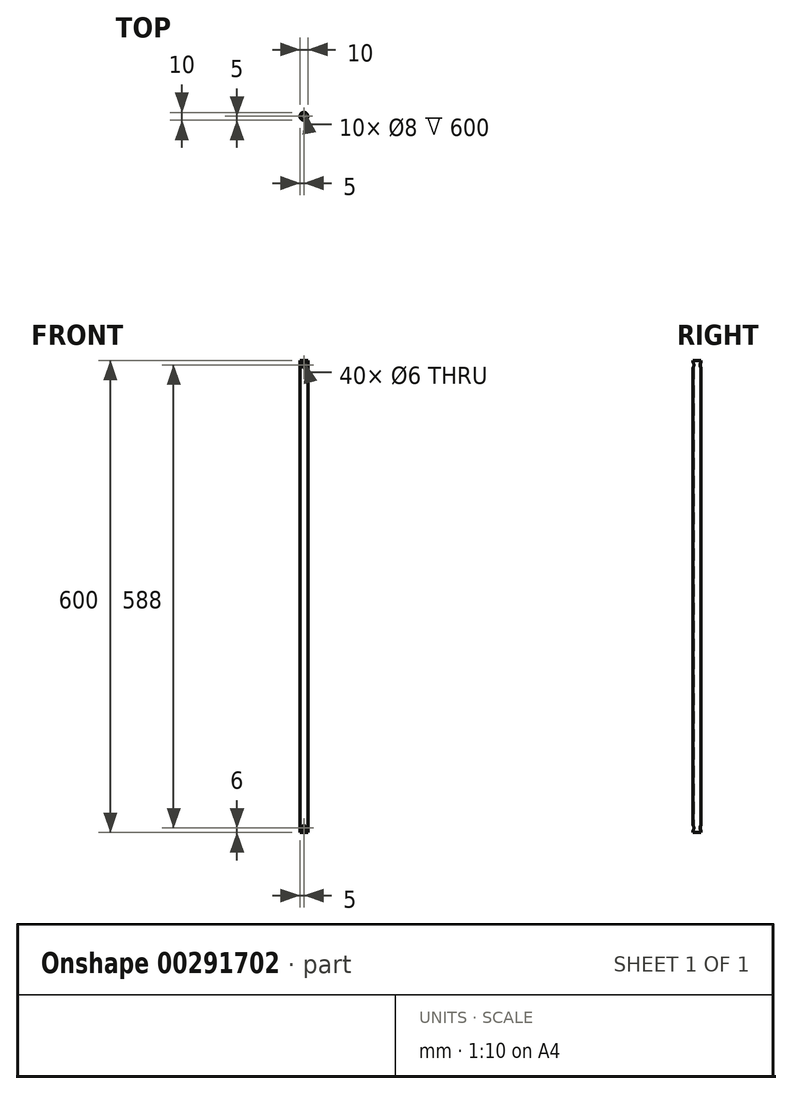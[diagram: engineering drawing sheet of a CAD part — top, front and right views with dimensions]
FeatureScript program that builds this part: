
annotation { "Feature Type Name" : "Feature", "Feature Type Description" : "" }
export const myFeature = defineFeature(function(context is Context, id is Id, definition is map)
    precondition{}
    {
        {
            var Q0;
            Q0=qCreatedBy(makeId("Top.planeOp"),FACE);
            var sketch = newSketch(context, id + "F0", { "sketchPlane" : qUnion([Q0])});
            skCircle(sketch, "E0", {"center": v(0, 0) * mm, "radius": 5 * mm});
            skCircle(sketch, "E1", {"center": v(0, 0) * mm, "radius": 4 * mm});
            skSolve(sketch);
        }
        {
            var Q0;
            Q0=qSketchRegion(id+"F0",true);
            extrude(context, id + "F1", {"entities" : qUnion([Q0]), "depth" : 600 * mm});
        }
        {
            var Q0;
            Q0=qCreatedBy(makeId("Front.planeOp"),FACE);
            var sketch = newSketch(context, id + "F2", { "sketchPlane" : qUnion([Q0])});
            skPoint(sketch, "E2", {"position": v(0, 6) * mm});
            skPoint(sketch, "E3", {"position": v(0, 594) * mm});
            skSolve(sketch);
        }
        {
            var Q0;
            Q0=sQuery(id+"F2.wireOp",VERTEX,"E2");
            var Q1;
            Q1=sQuery(id+"F2.wireOp",VERTEX,"E3");
            var Q2;
            Q2=makeQuery(id+"F1.opExtrude","SWEPT_BODY",BODY,{"disambiguationData":[OSD([sQuery(id+"F0.wireOp",EDGE,"E0"),sQuery(id+"F0.wireOp",EDGE,"E1")])]});
            hole(context, id + "F3", {"style" : HoleStyle.SIMPLE, "endStyle" : HoleEndStyle.THROUGH, "oppositeDirection" : true, "holeDiameter" : 6 * mm, "locations" : qUnion([Q0, Q1]), "scope" : qUnion([Q2]), "isTappedThrough" : true, "startStyle" : HoleStartStyle.PART});
        }
        {
            var Q0;
            Q0=sQuery(id+"F2.wireOp",VERTEX,"E3");
            var Q1;
            Q1=sQuery(id+"F2.wireOp",VERTEX,"E2");
            var Q2;
            Q2=makeQuery(id+"F1.opExtrude","SWEPT_BODY",BODY,{"disambiguationData":[OSD([sQuery(id+"F0.wireOp",EDGE,"E0"),sQuery(id+"F0.wireOp",EDGE,"E1")])]});
            hole(context, id + "F4", {"style" : HoleStyle.SIMPLE, "endStyle" : HoleEndStyle.THROUGH, "holeDiameter" : 6 * mm, "locations" : qUnion([Q0, Q1]), "scope" : qUnion([Q2]), "isTappedThrough" : true, "startStyle" : HoleStartStyle.PART});
        }
    });
